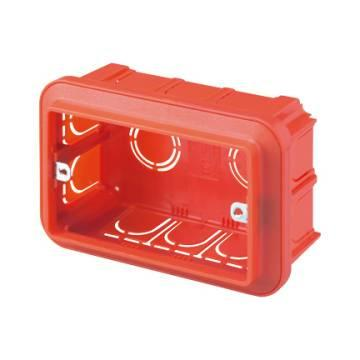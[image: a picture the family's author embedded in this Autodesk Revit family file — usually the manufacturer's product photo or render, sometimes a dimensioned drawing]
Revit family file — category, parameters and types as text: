
# Revit family: Building-FlushMountingEnclosures-GEWISS-24SC-BOXES_BIGBOX_3P_4P_6P
name_source: partatom
category: Apparecchi elettrici
revit_build: Autodesk Revit 2016 (Build: 20161004_0715(x64)
units: mm (PartAtom-declared; Revit-internal decimal feet)

## family parameters
Condiviso = Sì
Host = Superficie
Mantenere orientamento annotazione = Sì
Numero OmniClass = 23.80.30.14.24
Punto di calcolo locali = Sì
Quota connettore circolare = Usa diametro
Taglio con vuoti quando caricato = Sì
Tipo di parte = Normale
Titolo OmniClass = Junction Boxes

## types (3) — shared parameters
Catalogue = BUILDING
Catalogue Range = 24SC
Centro viti = 182 mm
Characteristics = Halogen free
Electrocod = 0210
For walls = Masonry
Glow Wire Test = 650°C
IDF = 4a0acd07-a30c-4abb-9a2e-c3177af7f6bf
IDT = 1294eac5-818f-4a58-8a02-802ca12f5010
Immagine tipo = GW24406.jpg
Incasso = 50 mm  [stored 0.164042 ft]
Installation = Flush mounting enclosures
Operating temperature = -15 ÷ +60°C
Produttore = GEWISS S.p.A.
Prospetto di default = 45 mm
SEO = Box
Technical sheet = https://www.gewiss.com
Thermo-pressure with ball = 70
Type of material = Halogen-free in compliance with EN 60754-2
Type: = High capacity
URL = https://www.gewiss.com
Version file RFA = 19.0

## per-type parameters (varying)
| type | Compartment pre-arrangement | Description: | Descrizione | EAN code | Fixing supports axles distance | Modello | No. SYSTEM modules | Outer dim. LxHxD (mm) |
| GW24404 - Box 4P | 4 | 4 gang | 4 GANG FLUSH MOUNTING BIG-BOX | 8011564444539 | 108,5MM | GW24404 | 4 gang | 144x85x50 |
| GW24406 - Box 6P | 6 | 6 gang | 6 GANG FLUSH MOUNTING BIG-BOX | 8011564444546 | 100MM | GW24406 | 6 gang | 194x90x50 |
| GW24403 - Box 3P | 3 | 3 gang | 3 GANG FLUSH MOUNTING BIG-BOX | 8011564444522 | 83,5MM | GW24403 | 3 gang | 119x80x50 |

note: source unit labels omitted for Thermo-pressure with ball — the stored unit's dimension contradicts the parameter name (converter mislabeling)

note: [stored X ft] marks values corroborated as IEEE doubles in the binary element streams (Revit-internal decimal feet)
